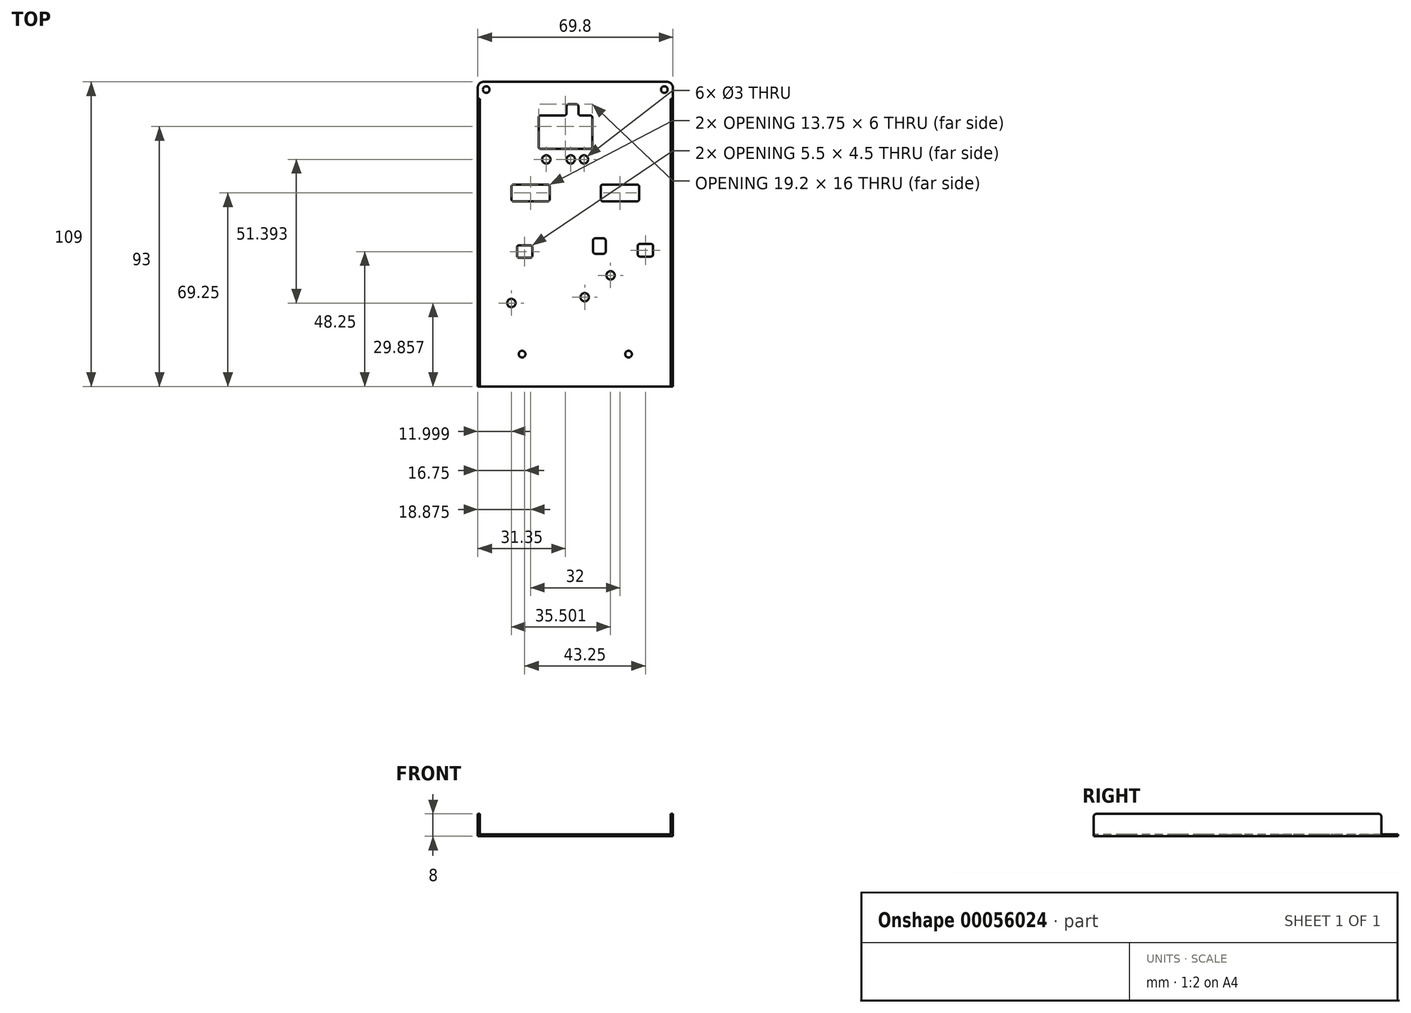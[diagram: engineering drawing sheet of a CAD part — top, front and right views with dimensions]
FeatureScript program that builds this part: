
annotation { "Feature Type Name" : "Feature", "Feature Type Description" : "" }
export const myFeature = defineFeature(function(context is Context, id is Id, definition is map)
    precondition{}
    {
        {
            var Q0;
            Q0=qCreatedBy(makeId("Top.planeOp"),FACE);
            var sketch = newSketch(context, id + "F0", { "sketchPlane" : qUnion([Q0])});
            skLineSegment(sketch, "E0", {"start": v(30.3, -54.5) * mm, "end": v(30.3, 52.5) * mm});
            skLineSegment(sketch, "E1", {"start": v(-39.5, -54.5) * mm, "end": v(-39.5, 52.5) * mm});
            skLineSegment(sketch, "E2", {"start": v(-37.5, 54.5) * mm, "end": v(28.3, 54.5) * mm});
            skLineSegment(sketch, "E3", {"start": v(-17.75, 31.25) * mm, "end": v(-17.75, 41.75) * mm});
            skLineSegment(sketch, "E4", {"start": v(4.5, 12.5) * mm, "end": v(4.5, 17) * mm});
            skLineSegment(sketch, "E5", {"start": v(5.25, 17.75) * mm, "end": v(17.5, 17.75) * mm});
            skLineSegment(sketch, "E6", {"start": v(5.25, 11.75) * mm, "end": v(17.5, 11.75) * mm});
            skLineSegment(sketch, "E7", {"start": v(18.25, 12.5) * mm, "end": v(18.25, 17) * mm});
            skLineSegment(sketch, "E8", {"start": v(-13.75, 12.5) * mm, "end": v(-13.75, 17) * mm});
            skLineSegment(sketch, "E9", {"start": v(-26.75, 11.75) * mm, "end": v(-14.5, 11.75) * mm});
            skLineSegment(sketch, "E10", {"start": v(-26.75, 17.75) * mm, "end": v(-14.5, 17.75) * mm});
            skLineSegment(sketch, "E11", {"start": v(-27.5, 12.5) * mm, "end": v(-27.5, 17) * mm});
            skLineSegment(sketch, "E12", {"start": v(18.5, -3.5) * mm, "end": v(22.5, -3.5) * mm});
            skLineSegment(sketch, "E13", {"start": v(23.25, -7.25) * mm, "end": v(23.25, -4.25) * mm});
            skLineSegment(sketch, "E14", {"start": v(17.75, -7.25) * mm, "end": v(17.75, -4.25) * mm});
            skLineSegment(sketch, "E15", {"start": v(18.5, -8) * mm, "end": v(22.5, -8) * mm});
            skLineSegment(sketch, "E16", {"start": v(-17, 42.5) * mm, "end": v(-8.5, 42.5) * mm});
            skLineSegment(sketch, "E17", {"start": v(1.45, 31.25) * mm, "end": v(1.45, 41.75) * mm});
            skLineSegment(sketch, "E18", {"start": v(-17, 30.5) * mm, "end": v(0.7, 30.5) * mm});
            skLineSegment(sketch, "E19", {"start": v(1.75, -6.25) * mm, "end": v(1.75, -2.25) * mm});
            skLineSegment(sketch, "E20", {"start": v(2.5, -1.5) * mm, "end": v(5.5, -1.5) * mm});
            skLineSegment(sketch, "E21", {"start": v(2.5, -7) * mm, "end": v(5.5, -7) * mm});
            skLineSegment(sketch, "E22", {"start": v(6.25, -6.25) * mm, "end": v(6.25, -2.25) * mm});
            skLineSegment(sketch, "E23", {"start": v(-24.75, -8.5) * mm, "end": v(-20.75, -8.5) * mm});
            skLineSegment(sketch, "E24", {"start": v(-25.5, -7.75) * mm, "end": v(-25.5, -4.75) * mm});
            skLineSegment(sketch, "E25", {"start": v(-20, -7.75) * mm, "end": v(-20, -4.75) * mm});
            skLineSegment(sketch, "E26", {"start": v(-24.75, -4) * mm, "end": v(-20.75, -4) * mm});
            skLineSegment(sketch, "E27", {"start": v(1.45, 41.25) * mm, "end": v(1.45, 41.75) * mm});
            skLineSegment(sketch, "E28", {"start": v(-2.75, 42.5) * mm, "end": v(0.7, 42.5) * mm});
            skLineSegment(sketch, "E29", {"start": v(-7.75, 43.25) * mm, "end": v(-7.75, 45.75) * mm});
            skLineSegment(sketch, "E30", {"start": v(-3.5, 43.25) * mm, "end": v(-3.5, 45.75) * mm});
            skLineSegment(sketch, "E31", {"start": v(-7, 46.5) * mm, "end": v(-4.25, 46.5) * mm});
            skLineSegment(sketch, "E32", {"start": v(-39.5, -54.5) * mm, "end": v(30.3, -54.5) * mm});
            skCircle(sketch, "E33", {"center": v(-36.5, 51.75) * mm, "radius": 1.2 * mm});
            skCircle(sketch, "E34", {"center": v(27.25, 51.75) * mm, "radius": 1.2 * mm});
            skCircle(sketch, "E35", {"center": v(14.45, -42.95) * mm, "radius": 1.2 * mm});
            skCircle(sketch, "E36", {"center": v(-23.65, -42.95) * mm, "radius": 1.2 * mm});
            skArc(sketch, "E37", {"start": v(-17, 42.5) * mm, "mid": v(-17.53, 42.28) * mm, "end": v(-17.75, 41.75) * mm});
            skArc(sketch, "E38", {"start": v(4.5, 12.5) * mm, "mid": v(4.72, 11.97) * mm, "end": v(5.25, 11.75) * mm});
            skArc(sketch, "E39", {"start": v(5.25, 17.75) * mm, "mid": v(4.72, 17.53) * mm, "end": v(4.5, 17) * mm});
            skArc(sketch, "E40", {"start": v(18.25, 17) * mm, "mid": v(18.03, 17.53) * mm, "end": v(17.5, 17.75) * mm});
            skArc(sketch, "E41", {"start": v(17.5, 11.75) * mm, "mid": v(18.03, 11.97) * mm, "end": v(18.25, 12.5) * mm});
            skArc(sketch, "E42", {"start": v(-14.5, 11.75) * mm, "mid": v(-13.97, 11.97) * mm, "end": v(-13.75, 12.5) * mm});
            skArc(sketch, "E43", {"start": v(-13.75, 17) * mm, "mid": v(-13.97, 17.53) * mm, "end": v(-14.5, 17.75) * mm});
            skArc(sketch, "E44", {"start": v(-26.75, 17.75) * mm, "mid": v(-27.28, 17.53) * mm, "end": v(-27.5, 17) * mm});
            skArc(sketch, "E45", {"start": v(-27.5, 12.5) * mm, "mid": v(-27.28, 11.97) * mm, "end": v(-26.75, 11.75) * mm});
            skArc(sketch, "E46", {"start": v(23.25, -4.25) * mm, "mid": v(23.03, -3.72) * mm, "end": v(22.5, -3.5) * mm});
            skArc(sketch, "E47", {"start": v(18.5, -3.5) * mm, "mid": v(17.97, -3.72) * mm, "end": v(17.75, -4.25) * mm});
            skArc(sketch, "E48", {"start": v(17.75, -7.25) * mm, "mid": v(17.97, -7.78) * mm, "end": v(18.5, -8) * mm});
            skArc(sketch, "E49", {"start": v(22.5, -8) * mm, "mid": v(23.03, -7.78) * mm, "end": v(23.25, -7.25) * mm});
            skArc(sketch, "E50", {"start": v(-17.75, 31.25) * mm, "mid": v(-17.53, 30.72) * mm, "end": v(-17, 30.5) * mm});
            skArc(sketch, "E51", {"start": v(0.7, 30.5) * mm, "mid": v(1.23, 30.72) * mm, "end": v(1.45, 31.25) * mm});
            skArc(sketch, "E52", {"start": v(1.75, -6.25) * mm, "mid": v(1.97, -6.78) * mm, "end": v(2.5, -7) * mm});
            skArc(sketch, "E53", {"start": v(2.5, -1.5) * mm, "mid": v(1.97, -1.72) * mm, "end": v(1.75, -2.25) * mm});
            skArc(sketch, "E54", {"start": v(6.25, -2.25) * mm, "mid": v(6.03, -1.72) * mm, "end": v(5.5, -1.5) * mm});
            skArc(sketch, "E55", {"start": v(5.5, -7) * mm, "mid": v(6.03, -6.78) * mm, "end": v(6.25, -6.25) * mm});
            skArc(sketch, "E56", {"start": v(-20.75, -8.5) * mm, "mid": v(-20.22, -8.28) * mm, "end": v(-20, -7.75) * mm});
            skArc(sketch, "E57", {"start": v(-25.5, -7.75) * mm, "mid": v(-25.28, -8.28) * mm, "end": v(-24.75, -8.5) * mm});
            skArc(sketch, "E58", {"start": v(-24.75, -4) * mm, "mid": v(-25.28, -4.22) * mm, "end": v(-25.5, -4.75) * mm});
            skArc(sketch, "E59", {"start": v(-20, -4.75) * mm, "mid": v(-20.22, -4.22) * mm, "end": v(-20.75, -4) * mm});
            skCircle(sketch, "E60", {"center": v(-1.25, -22.56) * mm, "radius": 1.5 * mm});
            skCircle(sketch, "E61", {"center": v(-27.5, -24.64) * mm, "radius": 1.5 * mm});
            skCircle(sketch, "E62", {"center": v(8, -14.75) * mm, "radius": 1.5 * mm});
            skCircle(sketch, "E63", {"center": v(-1.5, 26.75) * mm, "radius": 1.5 * mm});
            skCircle(sketch, "E64", {"center": v(-6.25, 26.75) * mm, "radius": 1.5 * mm});
            skCircle(sketch, "E65", {"center": v(-15, 26.75) * mm, "radius": 1.5 * mm});
            skArc(sketch, "E66", {"start": v(1.45, 41.75) * mm, "mid": v(1.23, 42.28) * mm, "end": v(0.7, 42.5) * mm});
            skArc(sketch, "E67", {"start": v(-7, 46.5) * mm, "mid": v(-7.53, 46.28) * mm, "end": v(-7.75, 45.75) * mm});
            skArc(sketch, "E68", {"start": v(-8.5, 42.5) * mm, "mid": v(-7.97, 42.72) * mm, "end": v(-7.75, 43.25) * mm});
            skArc(sketch, "E69", {"start": v(-3.5, 43.25) * mm, "mid": v(-3.28, 42.72) * mm, "end": v(-2.75, 42.5) * mm});
            skArc(sketch, "E70", {"start": v(-3.5, 45.75) * mm, "mid": v(-3.72, 46.28) * mm, "end": v(-4.25, 46.5) * mm});
            skPoint(sketch, "E71.visualSharp", {"position": v(-39.5, 54.5) * mm});
            skArc(sketch, "E71.filletArc", {"start": v(-37.5, 54.5) * mm, "mid": v(-38.91, 53.91) * mm, "end": v(-39.5, 52.5) * mm});
            skPoint(sketch, "E72.visualSharp", {"position": v(30.3, 54.5) * mm});
            skArc(sketch, "E72.filletArc", {"start": v(30.3, 52.5) * mm, "mid": v(29.71, 53.91) * mm, "end": v(28.3, 54.5) * mm});
            skSolve(sketch);
        }
        {
            var Q0;
            Q0 = qSketchRegion(id + "F0", true);
            extrude(context, id + "F1", {"entities" : qUnion([Q0]), "depth" : 0.74 * mm});
        }
        {
            var Q0;
            Q0=makeQuery(id+"F1.opExtrude","CAP_FACE",FACE,{"disambiguationData":[OSD([sQuery(id+"F0.wireOp",EDGE,"E0"),sQuery(id+"F0.wireOp",EDGE,"E1"),sQuery(id+"F0.wireOp",EDGE,"E2"),sQuery(id+"F0.wireOp",EDGE,"E3"),sQuery(id+"F0.wireOp",EDGE,"E4"),sQuery(id+"F0.wireOp",EDGE,"E5"),sQuery(id+"F0.wireOp",EDGE,"E6"),sQuery(id+"F0.wireOp",EDGE,"E7"),sQuery(id+"F0.wireOp",EDGE,"E8"),sQuery(id+"F0.wireOp",EDGE,"E9"),sQuery(id+"F0.wireOp",EDGE,"E10"),sQuery(id+"F0.wireOp",EDGE,"E11"),sQuery(id+"F0.wireOp",EDGE,"E12"),sQuery(id+"F0.wireOp",EDGE,"E13"),sQuery(id+"F0.wireOp",EDGE,"E14"),sQuery(id+"F0.wireOp",EDGE,"E15"),sQuery(id+"F0.wireOp",EDGE,"E16"),sQuery(id+"F0.wireOp",EDGE,"E17"),sQuery(id+"F0.wireOp",EDGE,"E18"),sQuery(id+"F0.wireOp",EDGE,"E19"),sQuery(id+"F0.wireOp",EDGE,"E20"),sQuery(id+"F0.wireOp",EDGE,"E21"),sQuery(id+"F0.wireOp",EDGE,"E22"),sQuery(id+"F0.wireOp",EDGE,"E23"),sQuery(id+"F0.wireOp",EDGE,"E24"),sQuery(id+"F0.wireOp",EDGE,"E25"),sQuery(id+"F0.wireOp",EDGE,"E26"),sQuery(id+"F0.wireOp",EDGE,"E27"),sQuery(id+"F0.wireOp",EDGE,"E28"),sQuery(id+"F0.wireOp",EDGE,"E29"),sQuery(id+"F0.wireOp",EDGE,"E30"),sQuery(id+"F0.wireOp",EDGE,"E31"),sQuery(id+"F0.wireOp",EDGE,"E32"),sQuery(id+"F0.wireOp",EDGE,"E33"),sQuery(id+"F0.wireOp",EDGE,"E34"),sQuery(id+"F0.wireOp",EDGE,"E35"),sQuery(id+"F0.wireOp",EDGE,"E36"),sQuery(id+"F0.wireOp",EDGE,"E37"),sQuery(id+"F0.wireOp",EDGE,"E38"),sQuery(id+"F0.wireOp",EDGE,"E39"),sQuery(id+"F0.wireOp",EDGE,"E40"),sQuery(id+"F0.wireOp",EDGE,"E41"),sQuery(id+"F0.wireOp",EDGE,"E42"),sQuery(id+"F0.wireOp",EDGE,"E43"),sQuery(id+"F0.wireOp",EDGE,"E44"),sQuery(id+"F0.wireOp",EDGE,"E45"),sQuery(id+"F0.wireOp",EDGE,"E46"),sQuery(id+"F0.wireOp",EDGE,"E47"),sQuery(id+"F0.wireOp",EDGE,"E48"),sQuery(id+"F0.wireOp",EDGE,"E49"),sQuery(id+"F0.wireOp",EDGE,"E50"),sQuery(id+"F0.wireOp",EDGE,"E51"),sQuery(id+"F0.wireOp",EDGE,"E52"),sQuery(id+"F0.wireOp",EDGE,"E53"),sQuery(id+"F0.wireOp",EDGE,"E54"),sQuery(id+"F0.wireOp",EDGE,"E55"),sQuery(id+"F0.wireOp",EDGE,"E56"),sQuery(id+"F0.wireOp",EDGE,"E57"),sQuery(id+"F0.wireOp",EDGE,"E58"),sQuery(id+"F0.wireOp",EDGE,"E59"),sQuery(id+"F0.wireOp",EDGE,"E60"),sQuery(id+"F0.wireOp",EDGE,"E61"),sQuery(id+"F0.wireOp",EDGE,"E62"),sQuery(id+"F0.wireOp",EDGE,"E63"),sQuery(id+"F0.wireOp",EDGE,"E64"),sQuery(id+"F0.wireOp",EDGE,"E65"),sQuery(id+"F0.wireOp",EDGE,"E66"),sQuery(id+"F0.wireOp",EDGE,"E67"),sQuery(id+"F0.wireOp",EDGE,"E68"),sQuery(id+"F0.wireOp",EDGE,"E69"),sQuery(id+"F0.wireOp",EDGE,"E70"),sQuery(id+"F0.wireOp",EDGE,"E71.filletArc"),sQuery(id+"F0.wireOp",EDGE,"E72.filletArc")])],"isStart":true});
            var sketch = newSketch(context, id + "F2", { "sketchPlane" : qUnion([Q0])});
            skLineSegment(sketch, "E73.bottom", {"start": v(30.3, 54.5) * mm, "end": v(29.56, 54.5) * mm});
            skLineSegment(sketch, "E73.top", {"start": v(30.3, -48.5) * mm, "end": v(29.56, -48.5) * mm});
            skLineSegment(sketch, "E73.left", {"start": v(30.3, 54.5) * mm, "end": v(30.3, -48.5) * mm});
            skLineSegment(sketch, "E73.right", {"start": v(29.56, 54.5) * mm, "end": v(29.56, -48.5) * mm});
            skLineSegment(sketch, "E74.bottom", {"start": v(-39.5, 54.5) * mm, "end": v(-38.76, 54.5) * mm});
            skLineSegment(sketch, "E74.top", {"start": v(-39.5, -48.5) * mm, "end": v(-38.76, -48.5) * mm});
            skLineSegment(sketch, "E74.left", {"start": v(-39.5, 54.5) * mm, "end": v(-39.5, -48.5) * mm});
            skLineSegment(sketch, "E74.right", {"start": v(-38.76, 54.5) * mm, "end": v(-38.76, -48.5) * mm});
            skSolve(sketch);
        }
        {
            var Q0;
            Q0 = qSketchRegion(id + "F2", true);
            extrude(context, id + "F3", {"entities" : qUnion([Q0]), "operationType" : NewBodyOperationType.ADD, "oppositeDirection" : true, "depth" : 8 * mm});
        }
        {
            var Q0;
            Q0=makeQuery(id+"F3.opExtrude","CAP_EDGE",EDGE,{"disambiguationData":[OSD([sQuery(id+"F2.wireOp",EDGE,"E73.bottom")])],"isStart":false});
            var Q1;
            Q1=makeQuery(id+"F3.opExtrude","CAP_EDGE",EDGE,{"disambiguationData":[OSD([sQuery(id+"F2.wireOp",EDGE,"E73.top")])],"isStart":false});
            var Q2;
            Q2=makeQuery(id+"F3.opExtrude","CAP_EDGE",EDGE,{"disambiguationData":[OSD([sQuery(id+"F2.wireOp",EDGE,"E74.top")])],"isStart":false});
            var Q3;
            Q3=makeQuery(id+"F3.opExtrude","CAP_EDGE",EDGE,{"disambiguationData":[OSD([sQuery(id+"F2.wireOp",EDGE,"E74.bottom")])],"isStart":false});
            fillet(context, id + "F4", {"entities" : qUnion([Q0, Q1, Q2, Q3]), "radius" : 1 * mm, "tangentPropagation" : true, "allowEdgeOverflow" : false});
        }
    });
